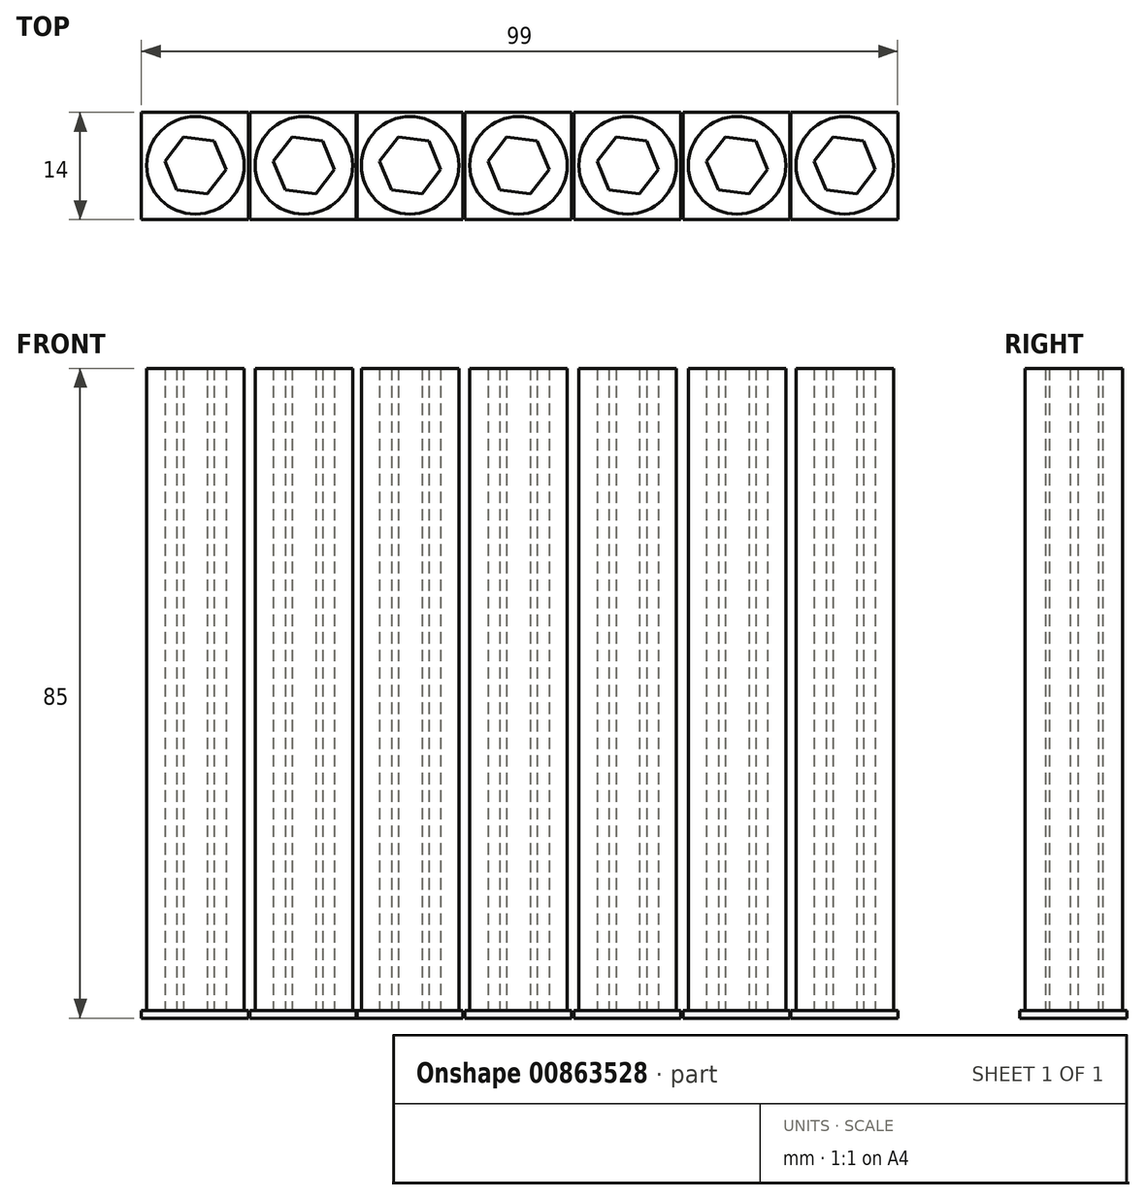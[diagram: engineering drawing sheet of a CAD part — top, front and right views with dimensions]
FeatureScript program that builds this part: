
annotation { "Feature Type Name" : "Feature", "Feature Type Description" : "" }
export const myFeature = defineFeature(function(context is Context, id is Id, definition is map)
    precondition{}
    {
        {
            var Q0;
            Q0=qCreatedBy(makeId("Top.planeOp"),FACE);
            var sketch = newSketch(context, id + "F0", { "sketchPlane" : qUnion([Q0])});
            skCircle(sketch, "E0.cCircle", {"center": v(-43.18, 23.94) * mm, "radius": 3.5 * mm, "construction": true});
            skLineSegment(sketch, "E0.0", {"start": v(-39.17, 23.42) * mm, "end": v(-41.63, 20.2) * mm});
            skLineSegment(sketch, "E0.1", {"start": v(-41.63, 20.2) * mm, "end": v(-45.63, 20.73) * mm});
            skLineSegment(sketch, "E0.2", {"start": v(-45.63, 20.73) * mm, "end": v(-47.19, 24.46) * mm});
            skLineSegment(sketch, "E0.3", {"start": v(-47.19, 24.46) * mm, "end": v(-44.73, 27.67) * mm});
            skLineSegment(sketch, "E0.4", {"start": v(-44.73, 27.67) * mm, "end": v(-40.72, 27.15) * mm});
            skLineSegment(sketch, "E0.5", {"start": v(-40.72, 27.15) * mm, "end": v(-39.17, 23.42) * mm});
            skPoint(sketch, "E0.0.midPoint", {"position": v(-40.4, 21.81) * mm});
            skCircle(sketch, "E1", {"center": v(-43.18, 23.94) * mm, "radius": 6.38 * mm});
            skSolve(sketch);
        }
        {
            var Q0;
            Q0=makeQuery(id+"F0.imprint","IMPRINT",FACE,{"disambiguationData":[TD([[makeQuery(id+"F0.imprint","IMPRINT",EDGE,{"derivedFrom":sQuery(id+"F0.wireOp",EDGE,"E0.0")}),1.0]])]});
            extrude(context, id + "F1", {"entities" : qUnion([Q0]), "depth" : 85 * mm, "offsetDistance" : 25 * mm});
        }
        {
            var Q0;
            Q0=qCreatedBy(makeId("Top.planeOp"),FACE);
            cPlane(context, id + "F2", {"entities" : qUnion([Q0]), "cplaneType" : CPlaneType.OFFSET, "offset" : 0 * mm, "oppositeDirection" : true, "width" : 150 * mm, "height" : 150 * mm});
        }
        {
            var Q0;
            Q0=qCreatedBy(id+"F2.planeOp",FACE);
            var sketch = newSketch(context, id + "F3", { "sketchPlane" : qUnion([Q0])});
            skLineSegment(sketch, "E2.bottom", {"start": v(-36.24, 30.86) * mm, "end": v(-50.24, 30.86) * mm});
            skLineSegment(sketch, "E2.top", {"start": v(-36.24, 16.86) * mm, "end": v(-50.24, 16.86) * mm});
            skLineSegment(sketch, "E2.left", {"start": v(-36.24, 30.86) * mm, "end": v(-36.24, 16.86) * mm});
            skLineSegment(sketch, "E2.right", {"start": v(-50.24, 30.86) * mm, "end": v(-50.24, 16.86) * mm});
            skPoint(sketch, "E2.middle", {"position": v(-43.24, 23.86) * mm});
            skSolve(sketch);
        }
        {
            var Q0;
            Q0=qSketchRegion(id+"F3",true);
            extrude(context, id + "F4", {"entities" : qUnion([Q0]), "operationType" : NewBodyOperationType.ADD, "depth" : 1 * mm, "offsetDistance" : 25 * mm});
        }
        {
            var Q0;
            Q0=makeQuery(id+"F1.opExtrude","SWEPT_BODY",BODY,{"disambiguationData":[OSD([sQuery(id+"F0.wireOp",EDGE,"E0.0"),sQuery(id+"F0.wireOp",EDGE,"E0.1"),sQuery(id+"F0.wireOp",EDGE,"E0.2"),sQuery(id+"F0.wireOp",EDGE,"E0.3"),sQuery(id+"F0.wireOp",EDGE,"E0.4"),sQuery(id+"F0.wireOp",EDGE,"E0.5"),sQuery(id+"F0.wireOp",EDGE,"E1")])]});
            transform(context, id + "F5", {"entities" : qUnion([Q0]), "transformType" : TransformType.TRANSLATION_3D, "dx" : 14.2 * mm, "dy" : 0 * mm, "dz" : 0 * mm, "makeCopy" : true});
        }
        {
            var Q0;
            Q0=makeQuery(id+"F5.opPattern","COPY",BODY,{"derivedFrom":makeQuery(id+"F1.opExtrude","SWEPT_BODY",BODY,{"disambiguationData":[OSD([sQuery(id+"F0.wireOp",EDGE,"E0.0"),sQuery(id+"F0.wireOp",EDGE,"E0.1"),sQuery(id+"F0.wireOp",EDGE,"E0.2"),sQuery(id+"F0.wireOp",EDGE,"E0.3"),sQuery(id+"F0.wireOp",EDGE,"E0.4"),sQuery(id+"F0.wireOp",EDGE,"E0.5"),sQuery(id+"F0.wireOp",EDGE,"E1")])]}),"instanceName":"1"});
            transform(context, id + "F6", {"entities" : qUnion([Q0]), "transformType" : TransformType.TRANSLATION_3D, "dx" : 13.9 * mm, "dy" : 0 * mm, "dz" : 0 * mm, "makeCopy" : true});
        }
        {
            var Q0;
            Q0=makeQuery(id+"F6.opPattern","COPY",BODY,{"derivedFrom":makeQuery(id+"F5.opPattern","COPY",BODY,{"derivedFrom":makeQuery(id+"F1.opExtrude","SWEPT_BODY",BODY,{"disambiguationData":[OSD([sQuery(id+"F0.wireOp",EDGE,"E0.0"),sQuery(id+"F0.wireOp",EDGE,"E0.1"),sQuery(id+"F0.wireOp",EDGE,"E0.2"),sQuery(id+"F0.wireOp",EDGE,"E0.3"),sQuery(id+"F0.wireOp",EDGE,"E0.4"),sQuery(id+"F0.wireOp",EDGE,"E0.5"),sQuery(id+"F0.wireOp",EDGE,"E1")])]}),"instanceName":"1"}),"instanceName":"1"});
            transform(context, id + "F7", {"entities" : qUnion([Q0]), "transformType" : TransformType.TRANSLATION_3D, "dx" : 14.2 * mm, "dy" : 0 * mm, "dz" : 0 * mm, "makeCopy" : true});
        }
        {
            var Q0;
            Q0=makeQuery(id+"F7.opPattern","COPY",BODY,{"derivedFrom":makeQuery(id+"F6.opPattern","COPY",BODY,{"derivedFrom":makeQuery(id+"F5.opPattern","COPY",BODY,{"derivedFrom":makeQuery(id+"F1.opExtrude","SWEPT_BODY",BODY,{"disambiguationData":[OSD([sQuery(id+"F0.wireOp",EDGE,"E0.0"),sQuery(id+"F0.wireOp",EDGE,"E0.1"),sQuery(id+"F0.wireOp",EDGE,"E0.2"),sQuery(id+"F0.wireOp",EDGE,"E0.3"),sQuery(id+"F0.wireOp",EDGE,"E0.4"),sQuery(id+"F0.wireOp",EDGE,"E0.5"),sQuery(id+"F0.wireOp",EDGE,"E1")])]}),"instanceName":"1"}),"instanceName":"1"}),"instanceName":"1"});
            transform(context, id + "F8", {"entities" : qUnion([Q0]), "transformType" : TransformType.TRANSLATION_3D, "dx" : 14.3 * mm, "dy" : 0 * mm, "dz" : 0 * mm, "makeCopy" : true});
        }
        {
            var Q0;
            Q0=makeQuery(id+"F8.opPattern","COPY",BODY,{"derivedFrom":makeQuery(id+"F7.opPattern","COPY",BODY,{"derivedFrom":makeQuery(id+"F6.opPattern","COPY",BODY,{"derivedFrom":makeQuery(id+"F5.opPattern","COPY",BODY,{"derivedFrom":makeQuery(id+"F1.opExtrude","SWEPT_BODY",BODY,{"disambiguationData":[OSD([sQuery(id+"F0.wireOp",EDGE,"E0.0"),sQuery(id+"F0.wireOp",EDGE,"E0.1"),sQuery(id+"F0.wireOp",EDGE,"E0.2"),sQuery(id+"F0.wireOp",EDGE,"E0.3"),sQuery(id+"F0.wireOp",EDGE,"E0.4"),sQuery(id+"F0.wireOp",EDGE,"E0.5"),sQuery(id+"F0.wireOp",EDGE,"E1")])]}),"instanceName":"1"}),"instanceName":"1"}),"instanceName":"1"}),"instanceName":"1"});
            transform(context, id + "F9", {"entities" : qUnion([Q0]), "transformType" : TransformType.TRANSLATION_3D, "dx" : 14.3 * mm, "dy" : 0 * mm, "dz" : 0 * mm, "makeCopy" : true});
        }
        {
            var Q0;
            Q0=makeQuery(id+"F9.opPattern","COPY",BODY,{"derivedFrom":makeQuery(id+"F8.opPattern","COPY",BODY,{"derivedFrom":makeQuery(id+"F7.opPattern","COPY",BODY,{"derivedFrom":makeQuery(id+"F6.opPattern","COPY",BODY,{"derivedFrom":makeQuery(id+"F5.opPattern","COPY",BODY,{"derivedFrom":makeQuery(id+"F1.opExtrude","SWEPT_BODY",BODY,{"disambiguationData":[OSD([sQuery(id+"F0.wireOp",EDGE,"E0.0"),sQuery(id+"F0.wireOp",EDGE,"E0.1"),sQuery(id+"F0.wireOp",EDGE,"E0.2"),sQuery(id+"F0.wireOp",EDGE,"E0.3"),sQuery(id+"F0.wireOp",EDGE,"E0.4"),sQuery(id+"F0.wireOp",EDGE,"E0.5"),sQuery(id+"F0.wireOp",EDGE,"E1")])]}),"instanceName":"1"}),"instanceName":"1"}),"instanceName":"1"}),"instanceName":"1"}),"instanceName":"1"});
            transform(context, id + "F10", {"entities" : qUnion([Q0]), "transformType" : TransformType.TRANSLATION_3D, "dx" : 14.1 * mm, "dy" : 0 * mm, "dz" : 0 * mm, "makeCopy" : true});
        }
    });
